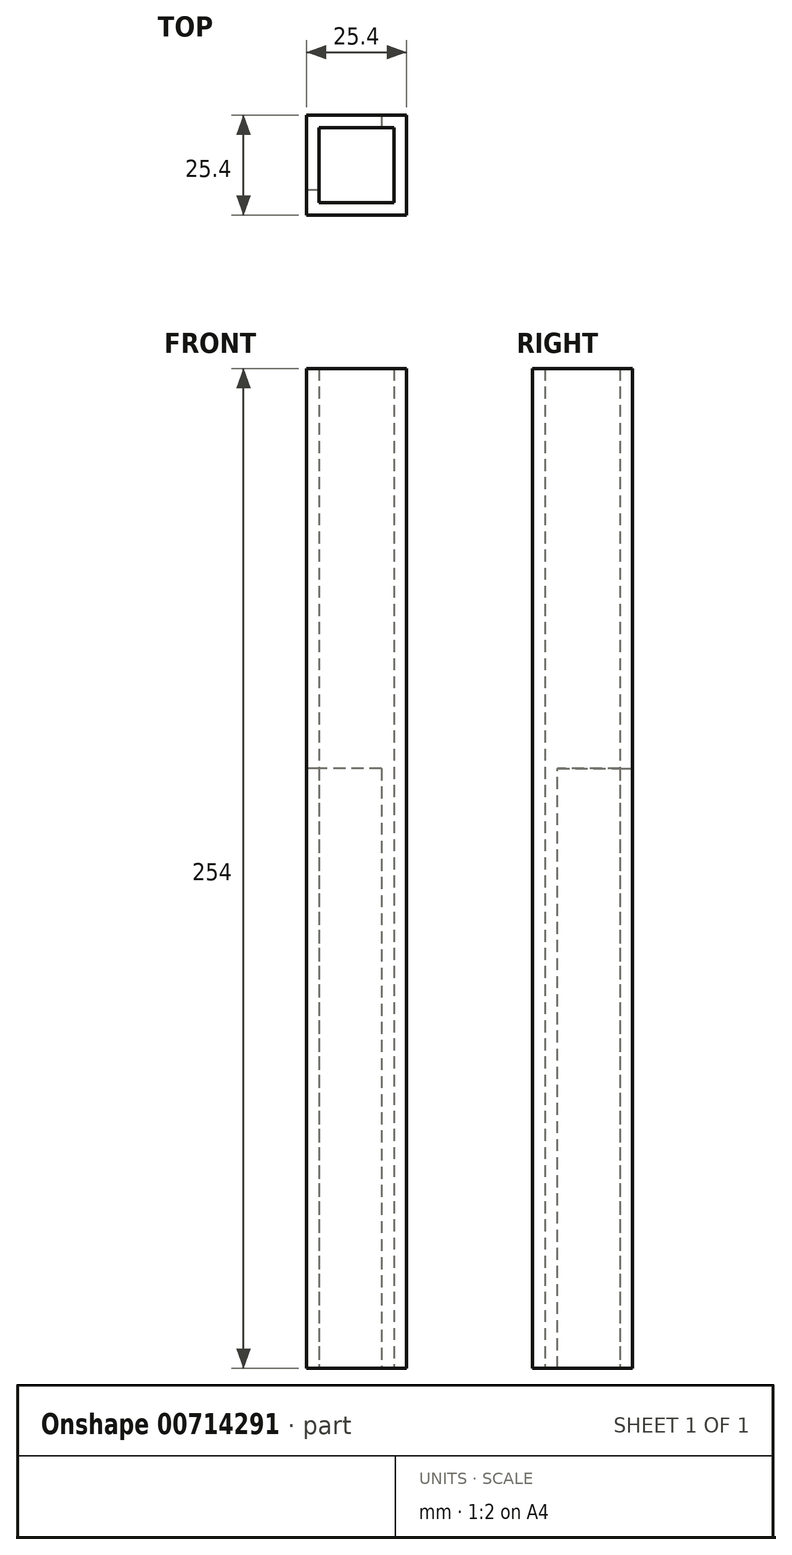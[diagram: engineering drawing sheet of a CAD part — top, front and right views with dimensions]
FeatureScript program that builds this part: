
annotation { "Feature Type Name" : "Feature", "Feature Type Description" : "" }
export const myFeature = defineFeature(function(context is Context, id is Id, definition is map)
    precondition{}
    {
        {
            var Q0;
            Q0=qCreatedBy(makeId("Top.planeOp"),FACE);
            var sketch = newSketch(context, id + "F0", { "sketchPlane" : qUnion([Q0])});
            skLineSegment(sketch, "E0.bottom", {"start": v(12.7, 12.7) * mm, "end": v(-12.7, 12.7) * mm});
            skLineSegment(sketch, "E0.top", {"start": v(12.7, -12.7) * mm, "end": v(-12.7, -12.7) * mm});
            skLineSegment(sketch, "E0.left", {"start": v(12.7, 12.7) * mm, "end": v(12.7, -12.7) * mm});
            skLineSegment(sketch, "E0.right", {"start": v(-12.7, 12.7) * mm, "end": v(-12.7, -12.7) * mm});
            skPoint(sketch, "E0.middle", {"position": v(0, 0) * mm});
            skLineSegment(sketch, "E1.0", {"start": v(9.53, -9.52) * mm, "end": v(-9.52, -9.52) * mm});
            skLineSegment(sketch, "E1.1", {"start": v(9.53, 9.52) * mm, "end": v(9.53, -9.52) * mm});
            skLineSegment(sketch, "E1.2", {"start": v(9.53, 9.52) * mm, "end": v(-9.52, 9.52) * mm});
            skLineSegment(sketch, "E1.3", {"start": v(-9.52, 9.52) * mm, "end": v(-9.52, -9.52) * mm});
            skSolve(sketch);
        }
        {
            var Q0;
            Q0 = qSketchRegion(id + "F0", true);
            extrude(context, id + "F1", {"entities" : qUnion([Q0]), "depth" : 254 * mm, "offsetDistance" : 25.4 * mm});
        }
        {
            var Q0;
            Q0=makeQuery(id+"F1.opExtrude","SWEPT_FACE",FACE,{"disambiguationData":[OSD([sQuery(id+"F0.wireOp",EDGE,"E0.right")])]});
            var sketch = newSketch(context, id + "F2", { "sketchPlane" : qUnion([Q0])});
            skLineSegment(sketch, "E2.0", {"start": v(-12.7, 0) * mm, "end": v(6.35, 0) * mm});
            skLineSegment(sketch, "E2.1", {"start": v(-12.7, 152.4) * mm, "end": v(-12.7, 0) * mm});
            skLineSegment(sketch, "E3", {"start": v(6.35, 0) * mm, "end": v(6.35, 152.4) * mm});
            skLineSegment(sketch, "E4", {"start": v(6.35, 152.4) * mm, "end": v(-12.7, 152.4) * mm});
            skPoint(sketch, "E5.orphan", {"position": v(12.7, 0) * mm});
            skPoint(sketch, "E6.orphan", {"position": v(-12.7, 254) * mm});
            skSolve(sketch);
        }
        {
            var Q0;
            Q0 = qSketchRegion(id + "F2", true);
            extrude(context, id + "F3", {"entities" : qUnion([Q0]), "operationType" : NewBodyOperationType.REMOVE, "oppositeDirection" : true, "depth" : 19.05 * mm, "offsetDistance" : 25.4 * mm});
        }
    });
